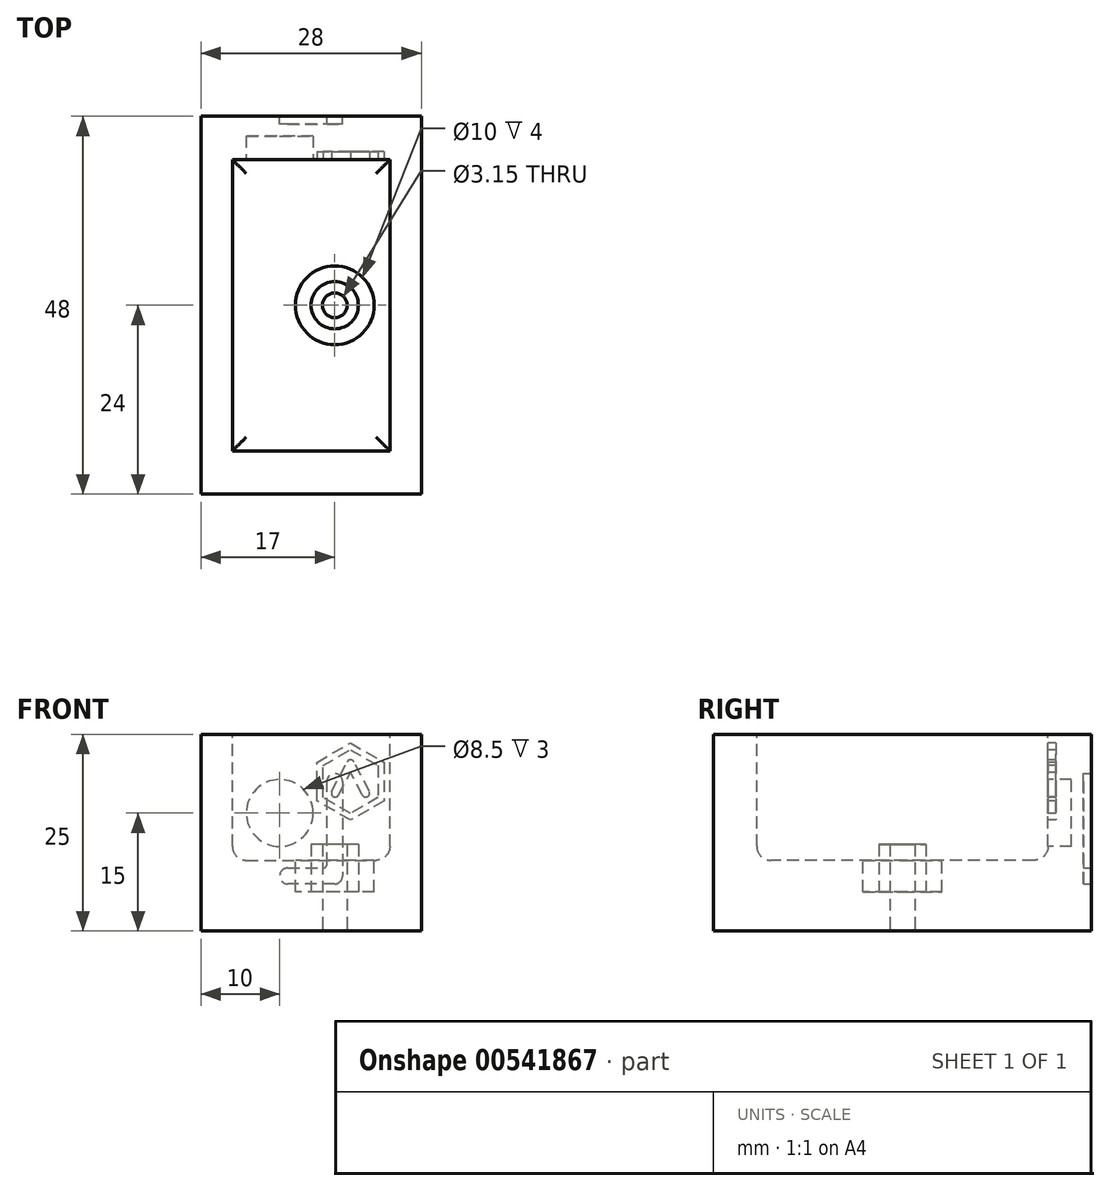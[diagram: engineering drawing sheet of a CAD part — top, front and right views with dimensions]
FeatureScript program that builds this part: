
annotation { "Feature Type Name" : "Feature", "Feature Type Description" : "" }
export const myFeature = defineFeature(function(context is Context, id is Id, definition is map)
    precondition{}
    {
        {
            var Q0;
            Q0=qCreatedBy(makeId("Top.planeOp"),FACE);
            var sketch = newSketch(context, id + "F0", { "sketchPlane" : qUnion([Q0])});
            skLineSegment(sketch, "E0.bottom", {"start": v(-28, 48) * mm, "end": v(0, 48) * mm});
            skLineSegment(sketch, "E0.top", {"start": v(-28, 0) * mm, "end": v(0, 0) * mm});
            skLineSegment(sketch, "E0.left", {"start": v(-28, 48) * mm, "end": v(-28, 0) * mm});
            skLineSegment(sketch, "E0.right", {"start": v(0, 48) * mm, "end": v(0, 0) * mm});
            skSolve(sketch);
        }
        {
            var Q0;
            Q0=makeQuery(id+"F0.imprint","IMPRINT",FACE,{"disambiguationData":[TD([[makeQuery(id+"F0.imprint","IMPRINT",EDGE,{"derivedFrom":sQuery(id+"F0.wireOp",EDGE,"E0.bottom")}),-1.0]])]});
            extrude(context, id + "F1", {"entities" : qUnion([Q0]), "depth" : 25 * mm, "offsetDistance" : 25 * mm});
        }
        {
            var Q0;
            Q0=makeQuery(id+"F1.opExtrude","CAP_FACE",FACE,{"disambiguationData":[OSD([sQuery(id+"F0.wireOp",EDGE,"E0.bottom"),sQuery(id+"F0.wireOp",EDGE,"E0.top"),sQuery(id+"F0.wireOp",EDGE,"E0.left"),sQuery(id+"F0.wireOp",EDGE,"E0.right")])],"isStart":false});
            var sketch = newSketch(context, id + "F2", { "sketchPlane" : qUnion([Q0])});
            skLineSegment(sketch, "E1.bottom", {"start": v(-24, 42.5) * mm, "end": v(-4, 42.5) * mm});
            skLineSegment(sketch, "E1.top", {"start": v(-24, 5.5) * mm, "end": v(-4, 5.5) * mm});
            skLineSegment(sketch, "E1.left", {"start": v(-24, 42.5) * mm, "end": v(-24, 5.5) * mm});
            skLineSegment(sketch, "E1.right", {"start": v(-4, 42.5) * mm, "end": v(-4, 5.5) * mm});
            skSolve(sketch);
        }
        {
            var Q0;
            Q0=qSketchRegion(id+"F2",true);
            extrude(context, id + "F3", {"entities" : qUnion([Q0]), "operationType" : NewBodyOperationType.REMOVE, "oppositeDirection" : true, "depth" : 16 * mm, "offsetDistance" : 25 * mm});
        }
        {
            var Q0;
            Q0=makeQuery(id+"F3.boolean.opBoolean","COPY",FACE,{"derivedFrom":makeQuery(id+"F3.opExtrude","CAP_FACE",FACE,{"disambiguationData":[OSD([sQuery(id+"F2.wireOp",EDGE,"E1.bottom"),sQuery(id+"F2.wireOp",EDGE,"E1.top"),sQuery(id+"F2.wireOp",EDGE,"E1.left"),sQuery(id+"F2.wireOp",EDGE,"E1.right")])],"isStart":false})});
            var sketch = newSketch(context, id + "F4", { "sketchPlane" : qUnion([Q0])});
            skCircle(sketch, "E2", {"center": v(-11, 24) * mm, "radius": 3 * mm});
            skCircle(sketch, "E3", {"center": v(-11, 24) * mm, "radius": 1.57 * mm});
            skSolve(sketch);
        }
        {
            var Q0;
            Q0=qSketchRegion(id+"F4",true);
            extrude(context, id + "F5", {"entities" : qUnion([Q0]), "operationType" : NewBodyOperationType.ADD, "depth" : 2 * mm, "offsetDistance" : 25 * mm});
        }
        {
            var Q0;
            {var subQ0=sQuery(id+"F2.wireOp",EDGE,"E1.right");var subQ1=sQuery(id+"F2.wireOp",EDGE,"E1.left");var subQ2=sQuery(id+"F2.wireOp",EDGE,"E1.top");var subQ3=sQuery(id+"F2.wireOp",EDGE,"E1.bottom");Q0=makeQuery(id+"F5.boolean.opBoolean","SPLIT",FACE,{"disambiguationData":[TD([makeQuery(id+"F3.boolean.opBoolean","COPY",FACE,{"derivedFrom":makeQuery(id+"F3.opExtrude","SWEPT_FACE",FACE,{"disambiguationData":[OSD([subQ3])]})})])],"derivedFrom":makeQuery(id+"F3.boolean.opBoolean","COPY",FACE,{"derivedFrom":makeQuery(id+"F3.opExtrude","CAP_FACE",FACE,{"disambiguationData":[OSD([subQ3,subQ2,subQ1,subQ0])],"isStart":false})})});}
            var sketch = newSketch(context, id + "F6", { "sketchPlane" : qUnion([Q0])});
            skCircle(sketch, "E4", {"center": v(-11, 24) * mm, "radius": 5 * mm});
            skCircle(sketch, "E5", {"center": v(-11, 24) * mm, "radius": 3 * mm});
            skSolve(sketch);
        }
        {
            var Q0;
            Q0=qSketchRegion(id+"F6",true);
            extrude(context, id + "F7", {"entities" : qUnion([Q0]), "operationType" : NewBodyOperationType.REMOVE, "oppositeDirection" : true, "depth" : 4 * mm, "offsetDistance" : 25 * mm});
        }
        {
            var Q0;
            Q0=makeQuery(id+"F3.boolean.opBoolean","COPY",FACE,{"derivedFrom":makeQuery(id+"F3.opExtrude","SWEPT_FACE",FACE,{"disambiguationData":[OSD([sQuery(id+"F2.wireOp",EDGE,"E1.top")])]})});
            var sketch = newSketch(context, id + "F8", { "sketchPlane" : qUnion([Q0])});
            skCircle(sketch, "E6", {"center": v(18, 15) * mm, "radius": 4.25 * mm});
            skSolve(sketch);
        }
        {
            var Q0;
            Q0=makeQuery(id+"F5.boolean.opBoolean","SPLIT",FACE,{"disambiguationData":[TD([makeQuery(id+"F5.opExtrude","SWEPT_FACE",FACE,{"disambiguationData":[OSD([sQuery(id+"F4.wireOp",EDGE,"E3")])]})])],"derivedFrom":makeQuery(id+"F3.boolean.opBoolean","COPY",FACE,{"derivedFrom":makeQuery(id+"F3.opExtrude","CAP_FACE",FACE,{"disambiguationData":[OSD([sQuery(id+"F2.wireOp",EDGE,"E1.bottom"),sQuery(id+"F2.wireOp",EDGE,"E1.top"),sQuery(id+"F2.wireOp",EDGE,"E1.left"),sQuery(id+"F2.wireOp",EDGE,"E1.right")])],"isStart":false})})});
            extrude(context, id + "F9", {"entities" : qUnion([Q0]), "operationType" : NewBodyOperationType.REMOVE, "endBound" : BoundingType.THROUGH_ALL, "oppositeDirection" : true, "depth" : 25 * mm, "offsetDistance" : 25 * mm});
        }
        {
            var Q0;
            Q0=makeQuery(id+"F3.boolean.opBoolean","COPY",FACE,{"derivedFrom":makeQuery(id+"F3.opExtrude","SWEPT_FACE",FACE,{"disambiguationData":[OSD([sQuery(id+"F2.wireOp",EDGE,"E1.bottom")])]})});
            var sketch = newSketch(context, id + "F10", { "sketchPlane" : qUnion([Q0])});
            skCircle(sketch, "E7", {"center": v(-18, 15) * mm, "radius": 4.25 * mm});
            skSolve(sketch);
        }
        {
            var Q0;
            Q0=makeQuery(id+"F10.imprint","IMPRINT",FACE,{"disambiguationData":[TD([[makeQuery(id+"F10.imprint","IMPRINT",EDGE,{"derivedFrom":sQuery(id+"F10.wireOp",EDGE,"E7")}),1.0]])]});
            extrude(context, id + "F11", {"entities" : qUnion([Q0]), "operationType" : NewBodyOperationType.REMOVE, "oppositeDirection" : true, "depth" : 3 * mm, "offsetDistance" : 25 * mm});
        }
        {
            var Q0;
            Q0=makeQuery(id+"F1.opExtrude","SWEPT_FACE",FACE,{"disambiguationData":[OSD([sQuery(id+"F0.wireOp",EDGE,"E0.bottom")])]});
            var sketch = newSketch(context, id + "F12", { "sketchPlane" : qUnion([Q0])});
            skLineSegment(sketch, "E8", {"start": v(10, 19) * mm, "end": v(10, 7) * mm});
            skLineSegment(sketch, "E9", {"start": v(11, 6) * mm, "end": v(17, 6) * mm});
            skLineSegment(sketch, "E10", {"start": v(18, 7) * mm, "end": v(18, 7) * mm});
            skLineSegment(sketch, "E11", {"start": v(17, 8) * mm, "end": v(12.5, 8) * mm});
            skLineSegment(sketch, "E12", {"start": v(12, 8.5) * mm, "end": v(12, 19) * mm});
            skLineSegment(sketch, "E13", {"start": v(11, 20) * mm, "end": v(11, 20) * mm});
            skPoint(sketch, "E14.visualSharp", {"position": v(10, 20) * mm});
            skArc(sketch, "E14.filletArc", {"start": v(11, 20) * mm, "mid": v(10.3, 19.7) * mm, "end": v(10, 19) * mm});
            skPoint(sketch, "E15.visualSharp", {"position": v(12, 20) * mm});
            skArc(sketch, "E15.filletArc", {"start": v(12, 19) * mm, "mid": v(11.7, 19.7) * mm, "end": v(11, 20) * mm});
            skPoint(sketch, "E16.visualSharp", {"position": v(10, 6) * mm});
            skArc(sketch, "E16.filletArc", {"start": v(10, 7) * mm, "mid": v(10.3, 6.3) * mm, "end": v(11, 6) * mm});
            skPoint(sketch, "E17.visualSharp", {"position": v(12, 8) * mm});
            skArc(sketch, "E17.filletArc", {"start": v(12, 8.5) * mm, "mid": v(12.15, 8.15) * mm, "end": v(12.5, 8) * mm});
            skPoint(sketch, "E18.visualSharp", {"position": v(18, 8) * mm});
            skArc(sketch, "E18.filletArc", {"start": v(18, 7) * mm, "mid": v(17.7, 7.7) * mm, "end": v(17, 8) * mm});
            skPoint(sketch, "E19.visualSharp", {"position": v(18, 6) * mm});
            skArc(sketch, "E19.filletArc", {"start": v(17, 6) * mm, "mid": v(17.7, 6.3) * mm, "end": v(18, 7) * mm});
            skSolve(sketch);
        }
        {
            var Q0;
            Q0 = qSketchRegion(id + "F12", true);
            extrude(context, id + "F13", {"entities" : qUnion([Q0]), "operationType" : NewBodyOperationType.REMOVE, "oppositeDirection" : true, "depth" : 1 * mm, "offsetDistance" : 25 * mm});
        }
        {
            var Q0;
            Q0=makeQuery(id+"F1.opExtrude","SWEPT_FACE",FACE,{"disambiguationData":[OSD([sQuery(id+"F0.wireOp",EDGE,"E0.top")])]});
            var sketch = newSketch(context, id + "F14", { "sketchPlane" : qUnion([Q0])});
            skLineSegment(sketch, "E20", {"start": v(-17, 7.3) * mm, "end": v(-17, 18.5) * mm});
            skLineSegment(sketch, "E21", {"start": v(-17, 18.5) * mm, "end": v(-11.8, 18.5) * mm});
            skLineSegment(sketch, "E22", {"start": v(-17, 16.5) * mm, "end": v(-11.8, 16.5) * mm});
            skLineSegment(sketch, "E23", {"start": v(-17, 18.5) * mm, "end": v(-18, 18.5) * mm});
            skLineSegment(sketch, "E24", {"start": v(-19, 17.5) * mm, "end": v(-19, 7.3) * mm});
            skLineSegment(sketch, "E25", {"start": v(-15, 14.5) * mm, "end": v(-11.8, 14.5) * mm});
            skArc(sketch, "E26", {"start": v(-11.8, 16.5) * mm, "mid": v(-10.8, 15.5) * mm, "end": v(-11.8, 14.5) * mm});
            skLineSegment(sketch, "E27", {"start": v(-15, 12.5) * mm, "end": v(-11.8, 12.5) * mm});
            skArc(sketch, "E28", {"start": v(-11.8, 18.5) * mm, "mid": v(-8.8, 15.5) * mm, "end": v(-11.8, 12.5) * mm});
            skArc(sketch, "E29", {"start": v(-19, 7.3) * mm, "mid": v(-18, 6.3) * mm, "end": v(-17, 7.3) * mm});
            skPoint(sketch, "E30.visualSharp", {"position": v(-19, 18.5) * mm});
            skArc(sketch, "E30.filletArc", {"start": v(-18, 18.5) * mm, "mid": v(-18.7, 18.2) * mm, "end": v(-19, 17.5) * mm});
            skCircle(sketch, "E31", {"center": v(-15, 13.5) * mm, "radius": 1 * mm});
            skLineSegment(sketch, "E32", {"start": v(-10.56, 6.66) * mm, "end": v(-9.03, 7.94) * mm, "construction": true});
            skLineSegment(sketch, "E33", {"start": v(-10.56, 6.66) * mm, "end": v(-15.77, 12.86) * mm});
            skLineSegment(sketch, "E34", {"start": v(-9.03, 7.94) * mm, "end": v(-14.23, 14.14) * mm});
            skArc(sketch, "E35", {"start": v(-10.56, 6.66) * mm, "mid": v(-9.16, 6.53) * mm, "end": v(-9.03, 7.94) * mm});
            skLineSegment(sketch, "E36", {"start": v(-8.8, 15.5) * mm, "end": v(-8.8, 7.3) * mm, "construction": true});
            skLineSegment(sketch, "E37", {"start": v(-8.8, 7.3) * mm, "end": v(-19, 7.3) * mm, "construction": true});
            skSolve(sketch);
        }
        {
            var Q0;
            Q0=makeQuery(id+"F3.boolean.opBoolean","COPY",FACE,{"derivedFrom":makeQuery(id+"F3.opExtrude","SWEPT_FACE",FACE,{"disambiguationData":[OSD([sQuery(id+"F2.wireOp",EDGE,"E1.bottom")])]})});
            var sketch = newSketch(context, id + "F15", { "sketchPlane" : qUnion([Q0])});
            skCircle(sketch, "E38.cCircle", {"center": v(-9, 19) * mm, "radius": 4.25 * mm, "construction": true});
            skLineSegment(sketch, "E38.0", {"start": v(-4.75, 16.55) * mm, "end": v(-9, 14.1) * mm});
            skLineSegment(sketch, "E38.1", {"start": v(-9, 14.1) * mm, "end": v(-13.25, 16.55) * mm});
            skLineSegment(sketch, "E38.2", {"start": v(-13.25, 16.55) * mm, "end": v(-13.25, 21.45) * mm});
            skLineSegment(sketch, "E38.3", {"start": v(-13.25, 21.45) * mm, "end": v(-9, 23.9) * mm});
            skLineSegment(sketch, "E38.4", {"start": v(-9, 23.9) * mm, "end": v(-4.75, 21.45) * mm});
            skLineSegment(sketch, "E38.5", {"start": v(-4.75, 21.45) * mm, "end": v(-4.75, 16.55) * mm});
            skPoint(sketch, "E38.0.midPoint", {"position": v(-6.87, 15.32) * mm});
            skCircle(sketch, "E39.cCircle", {"center": v(-9, 19) * mm, "radius": 3.5 * mm, "construction": true});
            skLineSegment(sketch, "E39.0", {"start": v(-12.5, 16.98) * mm, "end": v(-12.5, 21.02) * mm});
            skLineSegment(sketch, "E39.1", {"start": v(-12.5, 21.02) * mm, "end": v(-9, 23.04) * mm});
            skLineSegment(sketch, "E39.2", {"start": v(-9, 23.04) * mm, "end": v(-5.5, 21.02) * mm});
            skLineSegment(sketch, "E39.3", {"start": v(-5.5, 21.02) * mm, "end": v(-5.5, 16.98) * mm});
            skLineSegment(sketch, "E39.4", {"start": v(-5.5, 16.98) * mm, "end": v(-9, 14.96) * mm});
            skLineSegment(sketch, "E39.5", {"start": v(-9, 14.96) * mm, "end": v(-12.5, 16.98) * mm});
            skPoint(sketch, "E39.0.midPoint", {"position": v(-12.5, 19) * mm});
            skCircle(sketch, "E40", {"center": v(-9, 21.25) * mm, "radius": 0.5 * mm});
            skLineSegment(sketch, "E41", {"start": v(-11.38, 17.75) * mm, "end": v(-9.44, 21.48) * mm});
            skLineSegment(sketch, "E42", {"start": v(-6.62, 17.75) * mm, "end": v(-8.56, 21.48) * mm});
            skLineSegment(sketch, "E43", {"start": v(-11.38, 17.75) * mm, "end": v(-10.5, 17.3) * mm});
            skLineSegment(sketch, "E44", {"start": v(-7.5, 17.3) * mm, "end": v(-6.62, 17.75) * mm});
            skLineSegment(sketch, "E45", {"start": v(-10.5, 17.3) * mm, "end": v(-8.56, 21.02) * mm});
            skLineSegment(sketch, "E46", {"start": v(-7.5, 17.3) * mm, "end": v(-9.44, 21.02) * mm});
            skArc(sketch, "E47", {"start": v(-11.38, 17.75) * mm, "mid": v(-11.17, 17.08) * mm, "end": v(-10.5, 17.3) * mm});
            skArc(sketch, "E48", {"start": v(-6.62, 17.75) * mm, "mid": v(-6.83, 17.08) * mm, "end": v(-7.5, 17.3) * mm});
            skSolve(sketch);
        }
        {
            var Q0;
            Q0=makeQuery(id+"F3.boolean.opBoolean","COPY",FACE,{"derivedFrom":makeQuery(id+"F3.opExtrude","SWEPT_FACE",FACE,{"disambiguationData":[OSD([sQuery(id+"F2.wireOp",EDGE,"E1.top")])]})});
            var sketch = newSketch(context, id + "F16", { "sketchPlane" : qUnion([Q0])});
            skCircle(sketch, "E49.cCircle", {"center": v(9, 19) * mm, "radius": 4.25 * mm, "construction": true});
            skLineSegment(sketch, "E49.0", {"start": v(13.25, 16.55) * mm, "end": v(9, 14.1) * mm});
            skLineSegment(sketch, "E49.1", {"start": v(9, 14.1) * mm, "end": v(4.75, 16.55) * mm});
            skLineSegment(sketch, "E49.2", {"start": v(4.75, 16.55) * mm, "end": v(4.75, 21.45) * mm});
            skLineSegment(sketch, "E49.3", {"start": v(4.75, 21.45) * mm, "end": v(9, 23.9) * mm});
            skLineSegment(sketch, "E49.4", {"start": v(9, 23.9) * mm, "end": v(13.25, 21.45) * mm});
            skLineSegment(sketch, "E49.5", {"start": v(13.25, 21.45) * mm, "end": v(13.25, 16.55) * mm});
            skPoint(sketch, "E49.0.midPoint", {"position": v(11.12, 15.32) * mm});
            skCircle(sketch, "E50.cCircle", {"center": v(9, 19) * mm, "radius": 3.5 * mm, "construction": true});
            skLineSegment(sketch, "E50.0", {"start": v(5.5, 16.98) * mm, "end": v(5.5, 21.02) * mm});
            skLineSegment(sketch, "E50.1", {"start": v(5.5, 21.02) * mm, "end": v(9, 23.04) * mm});
            skLineSegment(sketch, "E50.2", {"start": v(9, 23.04) * mm, "end": v(12.5, 21.02) * mm});
            skLineSegment(sketch, "E50.3", {"start": v(12.5, 21.02) * mm, "end": v(12.5, 16.98) * mm});
            skLineSegment(sketch, "E50.4", {"start": v(12.5, 16.98) * mm, "end": v(9, 14.96) * mm});
            skLineSegment(sketch, "E50.5", {"start": v(9, 14.96) * mm, "end": v(5.5, 16.98) * mm});
            skPoint(sketch, "E50.0.midPoint", {"position": v(5.5, 19) * mm});
            skCircle(sketch, "E51", {"center": v(9, 21.25) * mm, "radius": 0.5 * mm});
            skLineSegment(sketch, "E52", {"start": v(6.62, 17.75) * mm, "end": v(8.56, 21.48) * mm});
            skLineSegment(sketch, "E53", {"start": v(11.38, 17.75) * mm, "end": v(9.44, 21.48) * mm});
            skLineSegment(sketch, "E54", {"start": v(6.62, 17.75) * mm, "end": v(7.5, 17.3) * mm});
            skLineSegment(sketch, "E55", {"start": v(10.5, 17.3) * mm, "end": v(11.38, 17.75) * mm});
            skLineSegment(sketch, "E56", {"start": v(7.5, 17.3) * mm, "end": v(9.44, 21.02) * mm});
            skLineSegment(sketch, "E57", {"start": v(10.5, 17.3) * mm, "end": v(8.56, 21.02) * mm});
            skArc(sketch, "E58", {"start": v(6.62, 17.75) * mm, "mid": v(6.83, 17.08) * mm, "end": v(7.5, 17.3) * mm});
            skArc(sketch, "E59", {"start": v(11.38, 17.75) * mm, "mid": v(11.17, 17.08) * mm, "end": v(10.5, 17.3) * mm});
            skSolve(sketch);
        }
        {
            var Q0;
            Q0 = qSketchRegion(id + "F15", true);
            var Q1;
            Q1=makeQuery(id+"F15.imprint","IMPRINT",FACE,{"disambiguationData":[TD([[makeQuery(id+"F15.imprint","IMPRINT",EDGE,{"derivedFrom":sQuery(id+"F15.wireOp",EDGE,"E43")}),-1.0]])]});
            var Q2;
            {var subQ4=sQuery(id+"F15.wireOp",EDGE,"E41");Q2=makeQuery(id+"F15.imprint","IMPRINT",FACE,{"disambiguationData":[TD([[makeQuery(id+"F15.imprint","IMPRINT",EDGE,{"derivedFrom":subQ4}),-1.0]])]});}
            var Q3;
            {var subQ0=sQuery(id+"F15.wireOp",EDGE,"E40");var subQ1=makeQuery(id+"F15.imprint","INTERSECT",VERTEX,{"derivedFrom":[subQ0,sQuery(id+"F15.wireOp",EDGE,"E41")]});Q3=makeQuery(id+"F15.imprint","IMPRINT",FACE,{"disambiguationData":[TD([[makeQuery(id+"F15.imprint","IMPRINT",EDGE,{"disambiguationData":[TD([[subQ1,1.0]])],"derivedFrom":subQ0}),1.0]])]});}
            var Q4;
            {var subQ0=sQuery(id+"F15.wireOp",EDGE,"E45");var subQ1=sQuery(id+"F15.wireOp",EDGE,"E40");var subQ2=makeQuery(id+"F15.imprint","INTERSECT",VERTEX,{"derivedFrom":[subQ1,subQ0]});Q4=makeQuery(id+"F15.imprint","IMPRINT",FACE,{"disambiguationData":[TD([[makeQuery(id+"F15.imprint","IMPRINT",EDGE,{"disambiguationData":[TD([[subQ2,1.0]])],"derivedFrom":subQ1}),-1.0]])]});}
            var Q5;
            {var subQ6=sQuery(id+"F15.wireOp",EDGE,"E42");Q5=makeQuery(id+"F15.imprint","IMPRINT",FACE,{"disambiguationData":[TD([[makeQuery(id+"F15.imprint","IMPRINT",EDGE,{"derivedFrom":subQ6}),1.0]])]});}
            var Q6;
            Q6=makeQuery(id+"F15.imprint","IMPRINT",FACE,{"disambiguationData":[TD([[makeQuery(id+"F15.imprint","IMPRINT",EDGE,{"derivedFrom":sQuery(id+"F15.wireOp",EDGE,"E44")}),-1.0]])]});
            extrude(context, id + "F17", {"entities" : qUnion([Q0, Q1, Q2, Q3, Q4, Q5, Q6]), "operationType" : NewBodyOperationType.REMOVE, "oppositeDirection" : true, "depth" : 1 * mm, "offsetDistance" : 25 * mm});
        }
        {
            var Q0;
            Q0=makeQuery(id+"F3.boolean.opBoolean","COPY",EDGE,{"derivedFrom":makeQuery(id+"F3.opExtrude","CAP_EDGE",EDGE,{"disambiguationData":[OSD([sQuery(id+"F2.wireOp",EDGE,"E1.left")])],"isStart":false})});
            var Q1;
            Q1=makeQuery(id+"F3.boolean.opBoolean","COPY",EDGE,{"derivedFrom":makeQuery(id+"F3.opExtrude","CAP_EDGE",EDGE,{"disambiguationData":[OSD([sQuery(id+"F2.wireOp",EDGE,"E1.bottom")])],"isStart":false})});
            var Q2;
            Q2=makeQuery(id+"F3.boolean.opBoolean","COPY",EDGE,{"derivedFrom":makeQuery(id+"F3.opExtrude","CAP_EDGE",EDGE,{"disambiguationData":[OSD([sQuery(id+"F2.wireOp",EDGE,"E1.right")])],"isStart":false})});
            var Q3;
            Q3=makeQuery(id+"F3.boolean.opBoolean","COPY",EDGE,{"derivedFrom":makeQuery(id+"F3.opExtrude","CAP_EDGE",EDGE,{"disambiguationData":[OSD([sQuery(id+"F2.wireOp",EDGE,"E1.top")])],"isStart":false})});
            fillet(context, id + "F18", {"entities" : qUnion([Q0, Q1, Q2, Q3]), "radius" : 1.75 * mm, "tangentPropagation" : true, "allowEdgeOverflow" : false});
        }
    });
